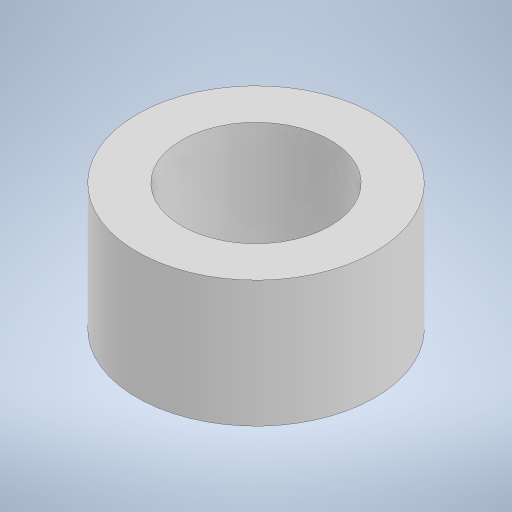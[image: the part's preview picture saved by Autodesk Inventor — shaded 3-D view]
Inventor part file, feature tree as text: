
AUTODESK INVENTOR PART (.ipt)
format: ipt  version: 2023.2 (Build 272271000, 271)  size: 208,384 bytes
history: native  units: mm
features: sketch x3, extrude x2, hole x1
ambient origin geometry x8: Origin, YZ Plane, XZ Plane, XY Plane, X Axis, Y Axis, Z Axis, Center Point
bodies: Solid1 (feature_tree)
feature tree (6):
  extrude  "Extrusion1"  Depth=7.5mm TaperAngle=0.0deg
  hole  "Hole1"  [1 undecoded]
  extrude  "Extrusion2"  Depth=0.75mm
  sketch  "Sketch1"  dims[d0=16.0mm d1=7.5mm d2=0.0mm]
  sketch  "Sketch2"  dims[d3=10.0mm d4=6.0mm d5=4.0mm d6=2.0mm d7=90.0deg d8=8.0mm d9=20.594885mm d10=1.0mm d11=0.0mm]
  sketch  "Sketch3"  dims[d12=0.0625mm d13=0.75mm d14=0.375mm]
note: 1 required parameter value undecoded (feature->parameter linkage not recoverable at this tier; creation-order binding heuristic only, values carry confidence <= 0.55)
